# Revit family: DTM30N6.1.24
name_source: partatom
category: Luminarias
units: mm (PartAtom-declared; Revit-internal decimal feet)

## family parameters
Compartido = No
Corte con vacíos al cargar = No
Cota de conector redondo = Diámetro de uso
Origen de luz = Sí
Punto de cálculo de habitación = No
Se basa en plano de trabajo = Sí
Siempre vertical = Sí
Tipo de pieza = Normal

## types (1)
- RECTANGULAR DWN RIEL_DTM30N6.1.24
    Archivo de red fotométrica = L646A-30W-840-B-24_IESNA95.IES
    Cambio de temperatura de color de luz atenuada = <Ninguno>
    Comentarios de vataje = 90-240V
    Descripción = LUMINARIA DOWNLIGHT EN FORMATO RECTANGULAR COMPATIBLE CON RIEL DE 6 ENTRADAS Y 3 CIRCUITOS, CUERPO DE ALUMINIO ACABADO EN COLOR NEGRO, IP 20, PESO 1.40Kg, TIPO DE LED 3030SMD PHILIPS CON 30.4W TOTAL, 1450 LUMENES, 90LM/W, IRC 90, TEMPERATURA EN BLANCO FRIO 4000K, 50 MIL HORAS DE VIDA PROMEDIO, APERTURA DE 24 GRADOS POR STOCK, ALIMENTADO A 90-240V
    Elevación por defecto = 1219 mm
    Fabricante = BRILLANT
    Filtro de color = 16777215
    Lámpara = 3030SMD PHILIPS
    Modelo = DTM30N6.1.24
    Watt per fixture = 15
    Ángulo de inclinación = 60.00°

## geometry (parser evidence)
native form markers: Blend x2
no freeform markers — native parametric forms only
